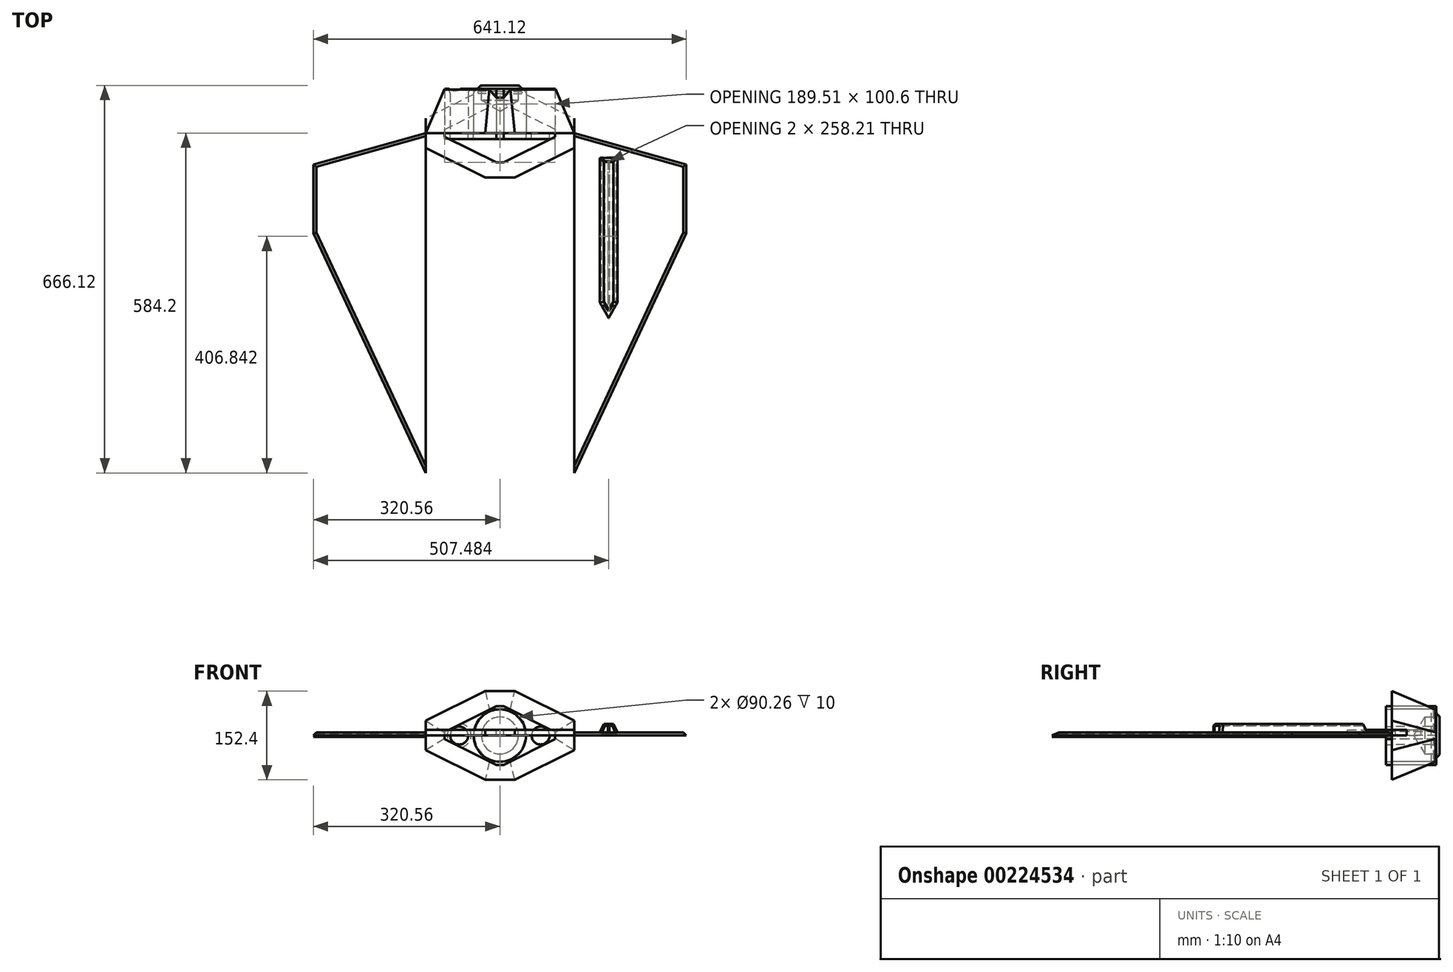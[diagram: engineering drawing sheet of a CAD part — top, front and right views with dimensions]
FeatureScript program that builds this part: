
annotation { "Feature Type Name" : "Feature", "Feature Type Description" : "" }
export const myFeature = defineFeature(function(context is Context, id is Id, definition is map)
    precondition{}
    {
        {
            var Q0;
            Q0=qCreatedBy(makeId("Top.planeOp"),FACE);
            var sketch = newSketch(context, id + "F0", { "sketchPlane" : qUnion([Q0])});
            skLineSegment(sketch, "E0", {"start": v(0, 0) * mm, "end": v(-127.58, 0) * mm});
            skLineSegment(sketch, "E1", {"start": v(0, 0) * mm, "end": v(0, -584.2) * mm});
            skLineSegment(sketch, "E2", {"start": v(0, -584.2) * mm, "end": v(-127.58, -584.2) * mm});
            skLineSegment(sketch, "E3", {"start": v(-127.58, -584.2) * mm, "end": v(-127.58, 0) * mm});
            skLineSegment(sketch, "E4", {"start": v(0, -584.2) * mm, "end": v(127.58, -584.2) * mm});
            skLineSegment(sketch, "E5", {"start": v(127.58, -584.2) * mm, "end": v(127.58, 0) * mm});
            skLineSegment(sketch, "E6", {"start": v(127.58, 0) * mm, "end": v(0, 0) * mm});
            skLineSegment(sketch, "E7", {"start": v(127.58, -584.2) * mm, "end": v(320.56, -172.08) * mm});
            skLineSegment(sketch, "E8", {"start": v(320.56, -172.08) * mm, "end": v(320.56, -53.88) * mm});
            skLineSegment(sketch, "E9", {"start": v(320.56, -53.88) * mm, "end": v(127.58, 0) * mm});
            skSolve(sketch);
        }
        {
            var Q0;
            Q0=makeQuery(id+"F0.imprint","IMPRINT",FACE,{"disambiguationData":[TD([[makeQuery(id+"F0.imprint","IMPRINT",EDGE,{"derivedFrom":sQuery(id+"F0.wireOp",EDGE,"E5")}),-1.0]])]});
            extrude(context, id + "F1", {"entities" : qUnion([Q0]), "depth" : 2.54 * mm, "hasSecondDirection" : true, "secondDirectionOppositeDirection" : true, "secondDirectionDepth" : 2.54 * mm});
        }
        {
            var Q0;
            Q0=makeQuery(id+"F1.opExtrude","CAP_EDGE",EDGE,{"disambiguationData":[OSD([sQuery(id+"F0.wireOp",EDGE,"E7")])],"isStart":false});
            var Q1;
            Q1=makeQuery(id+"F1.opExtrude","CAP_EDGE",EDGE,{"disambiguationData":[OSD([sQuery(id+"F0.wireOp",EDGE,"E8")])],"isStart":false});
            var Q2;
            Q2=makeQuery(id+"F1.opExtrude","CAP_EDGE",EDGE,{"disambiguationData":[OSD([sQuery(id+"F0.wireOp",EDGE,"E9")])],"isStart":false});
            chamfer(context, id + "F2", {"entities" : qUnion([Q0, Q1, Q2]), "width" : 5.08 * mm, "tangentPropagation" : true});
        }
        {
            var Q0;
            Q0=makeQuery(id+"F1.opExtrude","SWEPT_BODY",BODY,{"disambiguationData":[OSD([sQuery(id+"F0.wireOp",EDGE,"E5"),sQuery(id+"F0.wireOp",EDGE,"E7"),sQuery(id+"F0.wireOp",EDGE,"E8"),sQuery(id+"F0.wireOp",EDGE,"E9")])]});
            var Q1;
            Q1=qCreatedBy(makeId("Right.planeOp"),FACE);
            mirror(context, id + "F3", {"entities" : qUnion([Q0]), "mirrorPlane" : qUnion([Q1])});
        }
        {
            var Q0;
            Q0=qCreatedBy(makeId("Front.planeOp"),FACE);
            var sketch = newSketch(context, id + "F4", { "sketchPlane" : qUnion([Q0])});
            skLineSegment(sketch, "E10", {"start": v(-127.58, 0) * mm, "end": v(-127.58, 25.4) * mm});
            skLineSegment(sketch, "E11", {"start": v(0, 76.2) * mm, "end": v(-25.4, 76.2) * mm});
            skLineSegment(sketch, "E12", {"start": v(-25.4, 76.2) * mm, "end": v(-127.58, 25.4) * mm});
            skLineSegment(sketch, "E13.MirrorCS", {"start": v(-25.4, -76.2) * mm, "end": v(-127.58, -25.4) * mm});
            skLineSegment(sketch, "E14.MirrorCS", {"start": v(0, -76.2) * mm, "end": v(-25.4, -76.2) * mm});
            skLineSegment(sketch, "E15.MirrorCS", {"start": v(-127.58, 0) * mm, "end": v(-127.58, -25.4) * mm});
            skLineSegment(sketch, "E16.MirrorCS", {"start": v(0, 76.2) * mm, "end": v(25.4, 76.2) * mm});
            skLineSegment(sketch, "E17.MirrorCS", {"start": v(25.4, 76.2) * mm, "end": v(127.58, 25.4) * mm});
            skLineSegment(sketch, "E18.MirrorCS", {"start": v(127.58, 0) * mm, "end": v(127.58, -25.4) * mm});
            skLineSegment(sketch, "E19.MirrorCS", {"start": v(25.4, -76.2) * mm, "end": v(127.58, -25.4) * mm});
            skLineSegment(sketch, "E20.MirrorCS", {"start": v(0, -76.2) * mm, "end": v(25.4, -76.2) * mm});
            skLineSegment(sketch, "E21", {"start": v(94.75, 0) * mm, "end": v(94.75, 6.35) * mm});
            skLineSegment(sketch, "E22", {"start": v(94.75, 6.35) * mm, "end": v(6.35, 50.3) * mm});
            skLineSegment(sketch, "E23.MirrorCS", {"start": v(-94.75, 6.35) * mm, "end": v(-6.35, 50.3) * mm});
            skLineSegment(sketch, "E24.MirrorCS", {"start": v(94.75, -6.35) * mm, "end": v(6.35, -50.3) * mm});
            skLineSegment(sketch, "E25.MirrorCS", {"start": v(-94.75, -6.35) * mm, "end": v(-6.35, -50.3) * mm});
            skLineSegment(sketch, "E26", {"start": v(94.75, -6.35) * mm, "end": v(94.75, 6.35) * mm});
            skLineSegment(sketch, "E27", {"start": v(6.35, 50.3) * mm, "end": v(-6.35, 50.3) * mm});
            skLineSegment(sketch, "E28", {"start": v(-94.75, 6.35) * mm, "end": v(-94.75, -6.35) * mm});
            skLineSegment(sketch, "E29", {"start": v(-6.35, -50.3) * mm, "end": v(6.35, -50.3) * mm});
            skLineSegment(sketch, "E30", {"start": v(127.58, 25.4) * mm, "end": v(127.58, 0) * mm});
            skCircle(sketch, "E31", {"center": v(0, 0) * mm, "radius": 45.13 * mm});
            skLineSegment(sketch, "E32", {"start": v(94.75, 0) * mm, "end": v(45.13, 0) * mm});
            skCircle(sketch, "E33", {"center": v(69.94, 0) * mm, "radius": 15.42 * mm});
            skCircle(sketch, "E34.MirrorC", {"center": v(-69.94, 0) * mm, "radius": 15.42 * mm});
            skSolve(sketch);
        }
        {
            var Q0;
            Q0=makeQuery(id+"F4.imprint","IMPRINT",FACE,{"disambiguationData":[TD([[makeQuery(id+"F4.imprint","IMPRINT",EDGE,{"derivedFrom":sQuery(id+"F4.wireOp",EDGE,"E10")}),-1.0]])]});
            extrude(context, id + "F5", {"entities" : qUnion([Q0]), "oppositeDirection" : true, "depth" : 76.2 * mm});
        }
        {
            var Q0;
            Q0=makeQuery(id+"F5.opExtrude","CAP_EDGE",EDGE,{"disambiguationData":[OSD([sQuery(id+"F4.wireOp",EDGE,"E17.MirrorCS")])],"isStart":false});
            var Q1;
            Q1=makeQuery(id+"F5.opExtrude","CAP_EDGE",EDGE,{"disambiguationData":[OSD([sQuery(id+"F4.wireOp",EDGE,"E11"),sQuery(id+"F4.wireOp",EDGE,"E16.MirrorCS")])],"isStart":false});
            var Q2;
            Q2=makeQuery(id+"F5.opExtrude","CAP_EDGE",EDGE,{"disambiguationData":[OSD([sQuery(id+"F4.wireOp",EDGE,"E12")])],"isStart":false});
            var Q3;
            Q3=makeQuery(id+"F5.opExtrude","CAP_EDGE",EDGE,{"disambiguationData":[OSD([sQuery(id+"F4.wireOp",EDGE,"E10"),sQuery(id+"F4.wireOp",EDGE,"E15.MirrorCS")])],"isStart":false});
            var Q4;
            Q4=makeQuery(id+"F5.opExtrude","CAP_EDGE",EDGE,{"disambiguationData":[OSD([sQuery(id+"F4.wireOp",EDGE,"E13.MirrorCS")])],"isStart":false});
            var Q5;
            Q5=makeQuery(id+"F5.opExtrude","CAP_EDGE",EDGE,{"disambiguationData":[OSD([sQuery(id+"F4.wireOp",EDGE,"E14.MirrorCS"),sQuery(id+"F4.wireOp",EDGE,"E20.MirrorCS")])],"isStart":false});
            var Q6;
            Q6=makeQuery(id+"F5.opExtrude","CAP_EDGE",EDGE,{"disambiguationData":[OSD([sQuery(id+"F4.wireOp",EDGE,"E19.MirrorCS")])],"isStart":false});
            var Q7;
            Q7=makeQuery(id+"F5.opExtrude","CAP_EDGE",EDGE,{"disambiguationData":[OSD([sQuery(id+"F4.wireOp",EDGE,"E18.MirrorCS"),sQuery(id+"F4.wireOp",EDGE,"E30")])],"isStart":false});
            chamfer(context, id + "F6", {"entities" : qUnion([Q0, Q1, Q2, Q3, Q4, Q5, Q6, Q7]), "chamferType" : ChamferType.OFFSET_ANGLE, "width" : 76.2 * mm, "oppositeDirection" : true, "angle" : 23 * degree, "tangentPropagation" : true});
        }
        {
            var Q0;
            Q0=makeQuery(id+"F4.imprint","IMPRINT",FACE,{"disambiguationData":[TD([[makeQuery(id+"F4.imprint","IMPRINT",EDGE,{"derivedFrom":sQuery(id+"F4.wireOp",EDGE,"E31")}),1.0]])]});
            extrude(context, id + "F7", {"entities" : qUnion([Q0]), "oppositeDirection" : true, "depth" : 82.55 * mm});
        }
        {
            var Q0;
            {var subQ0=sQuery(id+"F4.wireOp",EDGE,"E33");var subQ1=sQuery(id+"F4.wireOp",EDGE,"E32");var subQ2=makeQuery(id+"F4.imprint","INTERSECT",VERTEX,{"disambiguationData":[OD(0.0)],"derivedFrom":[subQ1,subQ0]});Q0=makeQuery(id+"F4.imprint","IMPRINT",FACE,{"disambiguationData":[TD([[makeQuery(id+"F4.imprint","IMPRINT",EDGE,{"disambiguationData":[TD([[subQ2,1.0]])],"derivedFrom":subQ1}),-1.0]])]});}
            var Q1;
            {var subQ0=sQuery(id+"F4.wireOp",EDGE,"E33");var subQ1=sQuery(id+"F4.wireOp",EDGE,"E32");var subQ2=makeQuery(id+"F4.imprint","INTERSECT",VERTEX,{"disambiguationData":[OD(0.0)],"derivedFrom":[subQ1,subQ0]});Q1=makeQuery(id+"F4.imprint","IMPRINT",FACE,{"disambiguationData":[TD([[makeQuery(id+"F4.imprint","IMPRINT",EDGE,{"disambiguationData":[TD([[subQ2,1.0]])],"derivedFrom":subQ1}),1.0]])]});}
            var Q2;
            Q2=makeQuery(id+"F4.imprint","IMPRINT",FACE,{"disambiguationData":[TD([[makeQuery(id+"F4.imprint","IMPRINT",EDGE,{"derivedFrom":sQuery(id+"F4.wireOp",EDGE,"E34.MirrorC")}),-1.0]])]});
            extrude(context, id + "F8", {"entities" : qUnion([Q0, Q1, Q2]), "oppositeDirection" : true, "depth" : 76.2 * mm});
        }
        {
            var Q0;
            Q0=makeQuery(id+"F7.opExtrude","CAP_EDGE",EDGE,{"disambiguationData":[OSD([sQuery(id+"F4.wireOp",EDGE,"E31")])],"isStart":false});
            chamfer(context, id + "F9", {"entities" : qUnion([Q0]), "width" : 12.7 * mm, "tangentPropagation" : true});
        }
        {
            var Q0;
            {var subQ0=sQuery(id+"F4.wireOp",EDGE,"E31");Q0=makeQuery(id+"F9.opChamfer","BLEND_EDGE",EDGE,{"blendedFrom":[makeQuery(id+"F7.opExtrude","CAP_EDGE",EDGE,{"disambiguationData":[OSD([subQ0])],"isStart":false}),makeQuery(id+"F7.opExtrude","CAP_FACE",FACE,{"disambiguationData":[OSD([subQ0])],"isStart":false})],"blendedInto":[makeQuery(id+"F7.opExtrude","CAP_FACE",FACE,{"disambiguationData":[OSD([subQ0])],"isStart":false})]});}
            fillet(context, id + "F10", {"entities" : qUnion([Q0]), "radius" : 10.16 * mm, "tangentPropagation" : true, "allowEdgeOverflow" : false});
        }
        {
            var Q0;
            Q0=makeQuery(id+"F7.opExtrude","CAP_FACE",FACE,{"disambiguationData":[OSD([sQuery(id+"F4.wireOp",EDGE,"E31")])],"isStart":false});
            var sketch = newSketch(context, id + "F11", { "sketchPlane" : qUnion([Q0])});
            skPoint(sketch, "E35", {"position": v(0, 0) * mm});
            skSolve(sketch);
        }
        {
            var Q0;
            Q0=sQuery(id+"F11.wireOp",VERTEX,"E35");
            var Q1;
            Q1=makeQuery(id+"F7.opExtrude","SWEPT_BODY",BODY,{"disambiguationData":[OSD([sQuery(id+"F4.wireOp",EDGE,"E31")])]});
            hole(context, id + "F12", {"style" : HoleStyle.SIMPLE, "endStyle" : HoleEndStyle.BLIND, "holeDiameter" : 63.5 * mm, "holeDepth" : 25.4 * mm, "locations" : qUnion([Q0]), "scope" : qUnion([Q1])});
        }
        {
            var Q0;
            {var subQ0=sQuery(id+"F4.wireOp",EDGE,"E31");Q0=makeQuery(id+"F9.opChamfer","BLEND_EDGE",EDGE,{"blendedFrom":[makeQuery(id+"F7.opExtrude","CAP_EDGE",EDGE,{"disambiguationData":[OSD([subQ0])],"isStart":false}),makeQuery(id+"F7.opExtrude","SWEPT_FACE",FACE,{"disambiguationData":[OSD([subQ0])]})],"blendedInto":[makeQuery(id+"F7.opExtrude","SWEPT_FACE",FACE,{"disambiguationData":[OSD([subQ0])]})]});}
            chamfer(context, id + "F13", {"entities" : qUnion([Q0]), "width" : 5.08 * mm, "tangentPropagation" : true});
        }
        {
            var Q0;
            Q0=makeQuery(id+"F8.opExtrude","CAP_EDGE",EDGE,{"disambiguationData":[OSD([sQuery(id+"F4.wireOp",EDGE,"E33")])],"isStart":false});
            var Q1;
            Q1=makeQuery(id+"F8.opExtrude","CAP_EDGE",EDGE,{"disambiguationData":[OSD([sQuery(id+"F4.wireOp",EDGE,"E34.MirrorC")])],"isStart":false});
            chamfer(context, id + "F14", {"entities" : qUnion([Q0, Q1]), "width" : 5.08 * mm, "tangentPropagation" : true});
        }
        {
            var Q0;
            {var subQ0=sQuery(id+"F4.wireOp",EDGE,"E33");Q0=makeQuery(id+"F14.opChamfer","BLEND_EDGE",EDGE,{"blendedFrom":[makeQuery(id+"F8.opExtrude","CAP_EDGE",EDGE,{"disambiguationData":[OSD([subQ0])],"isStart":false}),makeQuery(id+"F8.opExtrude","SWEPT_FACE",FACE,{"disambiguationData":[OSD([subQ0])]})],"blendedInto":[makeQuery(id+"F8.opExtrude","SWEPT_FACE",FACE,{"disambiguationData":[OSD([subQ0])]})]});}
            var Q1;
            {var subQ0=sQuery(id+"F4.wireOp",EDGE,"E34.MirrorC");Q1=makeQuery(id+"F14.opChamfer","BLEND_EDGE",EDGE,{"blendedFrom":[makeQuery(id+"F8.opExtrude","CAP_EDGE",EDGE,{"disambiguationData":[OSD([subQ0])],"isStart":false}),makeQuery(id+"F8.opExtrude","SWEPT_FACE",FACE,{"disambiguationData":[OSD([subQ0])]})],"blendedInto":[makeQuery(id+"F8.opExtrude","SWEPT_FACE",FACE,{"disambiguationData":[OSD([subQ0])]})]});}
            fillet(context, id + "F15", {"entities" : qUnion([Q0, Q1]), "radius" : 7.62 * mm, "tangentPropagation" : true, "allowEdgeOverflow" : false});
        }
        {
            var Q0;
            Q0=makeQuery(id+"F8.opExtrude","CAP_FACE",FACE,{"disambiguationData":[OSD([sQuery(id+"F4.wireOp",EDGE,"E33")])],"isStart":false});
            var sketch = newSketch(context, id + "F16", { "sketchPlane" : qUnion([Q0])});
            skPoint(sketch, "E36", {"position": v(-69.94, 0) * mm});
            skSolve(sketch);
        }
        {
            var Q0;
            Q0=makeQuery(id+"F8.opExtrude","CAP_FACE",FACE,{"disambiguationData":[OSD([sQuery(id+"F4.wireOp",EDGE,"E34.MirrorC")])],"isStart":false});
            var sketch = newSketch(context, id + "F17", { "sketchPlane" : qUnion([Q0])});
            skPoint(sketch, "E37", {"position": v(69.94, 0) * mm});
            skSolve(sketch);
        }
        {
            var Q0;
            Q0=sQuery(id+"F16.wireOp",VERTEX,"E36");
            var Q1;
            Q1=sQuery(id+"F17.wireOp",VERTEX,"E37");
            var Q2;
            Q2=makeQuery(id+"F8.opExtrude","SWEPT_BODY",BODY,{"disambiguationData":[OSD([sQuery(id+"F4.wireOp",EDGE,"E33")])]});
            var Q3;
            Q3=makeQuery(id+"F8.opExtrude","SWEPT_BODY",BODY,{"disambiguationData":[OSD([sQuery(id+"F4.wireOp",EDGE,"E34.MirrorC")])]});
            hole(context, id + "F18", {"style" : HoleStyle.SIMPLE, "endStyle" : HoleEndStyle.BLIND, "holeDiameter" : 19.05 * mm, "holeDepth" : 19.05 * mm, "locations" : qUnion([Q0, Q1]), "scope" : qUnion([Q2, Q3])});
        }
        {
            var Q0;
            Q0=makeQuery(id+"F3.opPattern","COPY",BODY,{"derivedFrom":makeQuery(id+"F1.opExtrude","SWEPT_BODY",BODY,{"disambiguationData":[OSD([sQuery(id+"F0.wireOp",EDGE,"E5"),sQuery(id+"F0.wireOp",EDGE,"E7"),sQuery(id+"F0.wireOp",EDGE,"E8"),sQuery(id+"F0.wireOp",EDGE,"E9")])]}),"instanceName":"1"});
            transform(context, id + "F19", {"entities" : qUnion([Q0]), "transformType" : TransformType.TRANSLATION_3D, "dx" : 0 * mm, "dy" : 0 * mm, "dz" : 2.5 * mm, "makeCopy" : true});
        }
        {
            var Q0;
            Q0=makeQuery(id+"F1.opExtrude","SWEPT_BODY",BODY,{"disambiguationData":[OSD([sQuery(id+"F0.wireOp",EDGE,"E5"),sQuery(id+"F0.wireOp",EDGE,"E7"),sQuery(id+"F0.wireOp",EDGE,"E8"),sQuery(id+"F0.wireOp",EDGE,"E9")])]});
            transform(context, id + "F20", {"entities" : qUnion([Q0]), "transformType" : TransformType.TRANSLATION_3D, "dx" : 0 * mm, "dy" : 0 * mm, "dz" : 2.5 * mm, "makeCopy" : false});
        }
        {
            var Q0;
            Q0=makeQuery(id+"F5.opExtrude","CAP_FACE",FACE,{"disambiguationData":[OSD([sQuery(id+"F4.wireOp",EDGE,"E10"),sQuery(id+"F4.wireOp",EDGE,"E11"),sQuery(id+"F4.wireOp",EDGE,"E12"),sQuery(id+"F4.wireOp",EDGE,"E13.MirrorCS"),sQuery(id+"F4.wireOp",EDGE,"E14.MirrorCS"),sQuery(id+"F4.wireOp",EDGE,"E15.MirrorCS"),sQuery(id+"F4.wireOp",EDGE,"E16.MirrorCS"),sQuery(id+"F4.wireOp",EDGE,"E17.MirrorCS"),sQuery(id+"F4.wireOp",EDGE,"E18.MirrorCS"),sQuery(id+"F4.wireOp",EDGE,"E19.MirrorCS"),sQuery(id+"F4.wireOp",EDGE,"E20.MirrorCS"),sQuery(id+"F4.wireOp",EDGE,"E22"),sQuery(id+"F4.wireOp",EDGE,"E23.MirrorCS"),sQuery(id+"F4.wireOp",EDGE,"E24.MirrorCS"),sQuery(id+"F4.wireOp",EDGE,"E25.MirrorCS"),sQuery(id+"F4.wireOp",EDGE,"E26"),sQuery(id+"F4.wireOp",EDGE,"E27"),sQuery(id+"F4.wireOp",EDGE,"E28"),sQuery(id+"F4.wireOp",EDGE,"E29"),sQuery(id+"F4.wireOp",EDGE,"E30")])],"isStart":true});
            var Q1;
            Q1=makeQuery(id+"F7.opExtrude","CAP_FACE",FACE,{"disambiguationData":[OSD([sQuery(id+"F4.wireOp",EDGE,"E31")])],"isStart":true});
            var Q2;
            Q2=makeQuery(id+"F8.opExtrude","CAP_FACE",FACE,{"disambiguationData":[OSD([sQuery(id+"F4.wireOp",EDGE,"E34.MirrorC")])],"isStart":true});
            var Q3;
            Q3=makeQuery(id+"F8.opExtrude","CAP_FACE",FACE,{"disambiguationData":[OSD([sQuery(id+"F4.wireOp",EDGE,"E33")])],"isStart":true});
            var Q4;
            {var subQ1=sQuery(id+"F4.wireOp",EDGE,"E22");Q4=makeQuery(id+"F4.imprint","IMPRINT",FACE,{"disambiguationData":[TD([[makeQuery(id+"F4.imprint","IMPRINT",EDGE,{"derivedFrom":subQ1}),1.0]])]});}
            extrude(context, id + "F21", {"entities" : qUnion([Q0, Q1, Q2, Q3, Q4]), "depth" : 10 * mm});
        }
        {
            var Q0;
            Q0=makeQuery(id+"F21.opExtrude","SWEPT_BODY",BODY,{"disambiguationData":[OSD([sQuery(id+"F4.wireOp",EDGE,"E10"),sQuery(id+"F4.wireOp",EDGE,"E11"),sQuery(id+"F4.wireOp",EDGE,"E12"),sQuery(id+"F4.wireOp",EDGE,"E13.MirrorCS"),sQuery(id+"F4.wireOp",EDGE,"E14.MirrorCS"),sQuery(id+"F4.wireOp",EDGE,"E15.MirrorCS"),sQuery(id+"F4.wireOp",EDGE,"E16.MirrorCS"),sQuery(id+"F4.wireOp",EDGE,"E17.MirrorCS"),sQuery(id+"F4.wireOp",EDGE,"E18.MirrorCS"),sQuery(id+"F4.wireOp",EDGE,"E19.MirrorCS"),sQuery(id+"F4.wireOp",EDGE,"E20.MirrorCS"),sQuery(id+"F4.wireOp",EDGE,"E22"),sQuery(id+"F4.wireOp",EDGE,"E23.MirrorCS"),sQuery(id+"F4.wireOp",EDGE,"E24.MirrorCS"),sQuery(id+"F4.wireOp",EDGE,"E25.MirrorCS"),sQuery(id+"F4.wireOp",EDGE,"E26"),sQuery(id+"F4.wireOp",EDGE,"E27"),sQuery(id+"F4.wireOp",EDGE,"E28"),sQuery(id+"F4.wireOp",EDGE,"E29"),sQuery(id+"F4.wireOp",EDGE,"E30")])]});
            var Q1;
            Q1=sQuery(id+"F0.wireOp",EDGE,"E0");
            transform(context, id + "F22", {"entities" : qUnion([Q0]), "transformType" : TransformType.ROTATION, "transformAxis" : qUnion([Q1]), "angle" : 90 * degree, "oppositeDirection" : true, "makeCopy" : false});
        }
        {
            var Q0;
            Q0=makeQuery(id+"F21.opExtrude","SWEPT_BODY",BODY,{"disambiguationData":[OSD([sQuery(id+"F4.wireOp",EDGE,"E10"),sQuery(id+"F4.wireOp",EDGE,"E11"),sQuery(id+"F4.wireOp",EDGE,"E12"),sQuery(id+"F4.wireOp",EDGE,"E13.MirrorCS"),sQuery(id+"F4.wireOp",EDGE,"E14.MirrorCS"),sQuery(id+"F4.wireOp",EDGE,"E15.MirrorCS"),sQuery(id+"F4.wireOp",EDGE,"E16.MirrorCS"),sQuery(id+"F4.wireOp",EDGE,"E17.MirrorCS"),sQuery(id+"F4.wireOp",EDGE,"E18.MirrorCS"),sQuery(id+"F4.wireOp",EDGE,"E19.MirrorCS"),sQuery(id+"F4.wireOp",EDGE,"E20.MirrorCS"),sQuery(id+"F4.wireOp",EDGE,"E22"),sQuery(id+"F4.wireOp",EDGE,"E23.MirrorCS"),sQuery(id+"F4.wireOp",EDGE,"E24.MirrorCS"),sQuery(id+"F4.wireOp",EDGE,"E25.MirrorCS"),sQuery(id+"F4.wireOp",EDGE,"E26"),sQuery(id+"F4.wireOp",EDGE,"E27"),sQuery(id+"F4.wireOp",EDGE,"E28"),sQuery(id+"F4.wireOp",EDGE,"E29"),sQuery(id+"F4.wireOp",EDGE,"E30")])]});
            transform(context, id + "F23", {"entities" : qUnion([Q0]), "transformType" : TransformType.TRANSLATION_3D, "dx" : 0 * mm, "dy" : 0 * mm, "dz" : 10 * mm, "makeCopy" : false});
        }
        {
            var Q0;
            Q0=makeQuery(id+"F1.opExtrude","CAP_FACE",FACE,{"disambiguationData":[OSD([sQuery(id+"F0.wireOp",EDGE,"E5"),sQuery(id+"F0.wireOp",EDGE,"E7"),sQuery(id+"F0.wireOp",EDGE,"E8"),sQuery(id+"F0.wireOp",EDGE,"E9")])],"isStart":false});
            var sketch = newSketch(context, id + "F24", { "sketchPlane" : qUnion([Q0])});
            skLineSegment(sketch, "E38", {"start": v(171.92, -317.66) * mm, "end": v(186.92, -317.66) * mm});
            skLineSegment(sketch, "E39", {"start": v(186.92, -317.66) * mm, "end": v(201.92, -317.66) * mm});
            skLineSegment(sketch, "E40", {"start": v(201.92, -317.66) * mm, "end": v(201.92, -42.66) * mm});
            skLineSegment(sketch, "E41.MirrorCS", {"start": v(171.92, -317.66) * mm, "end": v(171.92, -42.66) * mm});
            skLineSegment(sketch, "E42", {"start": v(171.92, -42.66) * mm, "end": v(201.92, -42.66) * mm});
            skLineSegment(sketch, "E43", {"start": v(186.92, -42.66) * mm, "end": v(186.92, -317.66) * mm});
            skLineSegment(sketch, "E44", {"start": v(186.92, -317.66) * mm, "end": v(171.92, -291.67) * mm});
            skLineSegment(sketch, "E45.MirrorCS", {"start": v(186.92, -317.66) * mm, "end": v(201.92, -291.67) * mm});
            skSolve(sketch);
        }
        {
            var Q0;
            {var subQ4=sQuery(id+"F24.wireOp",EDGE,"E43");Q0=makeQuery(id+"F24.imprint","IMPRINT",FACE,{"disambiguationData":[TD([[makeQuery(id+"F24.imprint","IMPRINT",EDGE,{"derivedFrom":subQ4}),-1.0]])]});}
            var Q1;
            {var subQ4=sQuery(id+"F24.wireOp",EDGE,"E43");Q1=makeQuery(id+"F24.imprint","IMPRINT",FACE,{"disambiguationData":[TD([[makeQuery(id+"F24.imprint","IMPRINT",EDGE,{"derivedFrom":subQ4}),1.0]])]});}
            extrude(context, id + "F25", {"entities" : qUnion([Q0, Q1]), "operationType" : NewBodyOperationType.ADD, "depth" : 15 * mm, "hasDraft" : true, "draftAngle" : 25 * degree, "draftPullDirection" : true});
        }
        {
            var Q0;
            Q0=makeQuery(id+"F25.opExtrude","SWEPT_FACE",FACE,{"disambiguationData":[OSD([sQuery(id+"F24.wireOp",EDGE,"E44")])]});
            var Q1;
            Q1=makeQuery(id+"F25.opExtrude","SWEPT_FACE",FACE,{"disambiguationData":[OSD([sQuery(id+"F24.wireOp",EDGE,"E45.MirrorCS")])]});
            var Q2;
            Q2=makeQuery(id+"F25.opExtrude","SWEPT_FACE",FACE,{"disambiguationData":[OSD([sQuery(id+"F24.wireOp",EDGE,"E42")])]});
            shell(context, id + "F26", {"entities" : qUnion([Q0, Q1, Q2]), "thickness" : 3 * mm});
        }
        {
            var Q0;
            Q0=makeQuery(id+"F26.opShell","OFFSET_FACE",FACE,{"disambiguationData":[OSD([sQuery(id+"F0.wireOp",EDGE,"E5"),sQuery(id+"F0.wireOp",EDGE,"E7"),sQuery(id+"F0.wireOp",EDGE,"E8"),sQuery(id+"F0.wireOp",EDGE,"E9")])]});
            var sketch = newSketch(context, id + "F27", { "sketchPlane" : qUnion([Q0])});
            skLineSegment(sketch, "E46", {"start": v(186.92, -306.46) * mm, "end": v(186.92, -48.25) * mm});
            skLineSegment(sketch, "E47", {"start": v(186.92, -48.25) * mm, "end": v(187.92, -48.25) * mm});
            skLineSegment(sketch, "E48", {"start": v(186.92, -48.25) * mm, "end": v(185.92, -48.25) * mm});
            skLineSegment(sketch, "E49", {"start": v(185.92, -48.25) * mm, "end": v(185.92, -304.7) * mm});
            skLineSegment(sketch, "E50", {"start": v(185.92, -304.7) * mm, "end": v(186.92, -306.46) * mm});
            skLineSegment(sketch, "E51.MirrorCS", {"start": v(187.92, -48.25) * mm, "end": v(187.92, -304.7) * mm});
            skLineSegment(sketch, "E52.MirrorCS", {"start": v(187.92, -304.7) * mm, "end": v(186.92, -306.46) * mm});
            skSolve(sketch);
        }
        {
            var Q0;
            Q0 = qSketchRegion(id + "F27", true);
            var Q1;
            Q1=makeQuery(id+"F26.opShell","OFFSET_FACE",FACE,{"disambiguationData":[OSD([sQuery(id+"F24.wireOp",EDGE,"E40"),sQuery(id+"F24.wireOp",EDGE,"E41.MirrorCS"),sQuery(id+"F24.wireOp",EDGE,"E42"),sQuery(id+"F24.wireOp",EDGE,"E44"),sQuery(id+"F24.wireOp",EDGE,"E45.MirrorCS")])]});
            extrude(context, id + "F28", {"entities" : qUnion([Q0]), "operationType" : NewBodyOperationType.ADD, "endBound" : BoundingType.UP_TO_SURFACE, "endBoundEntityFace" : qUnion([Q1]), "depth" : 15 * mm});
        }
    });
